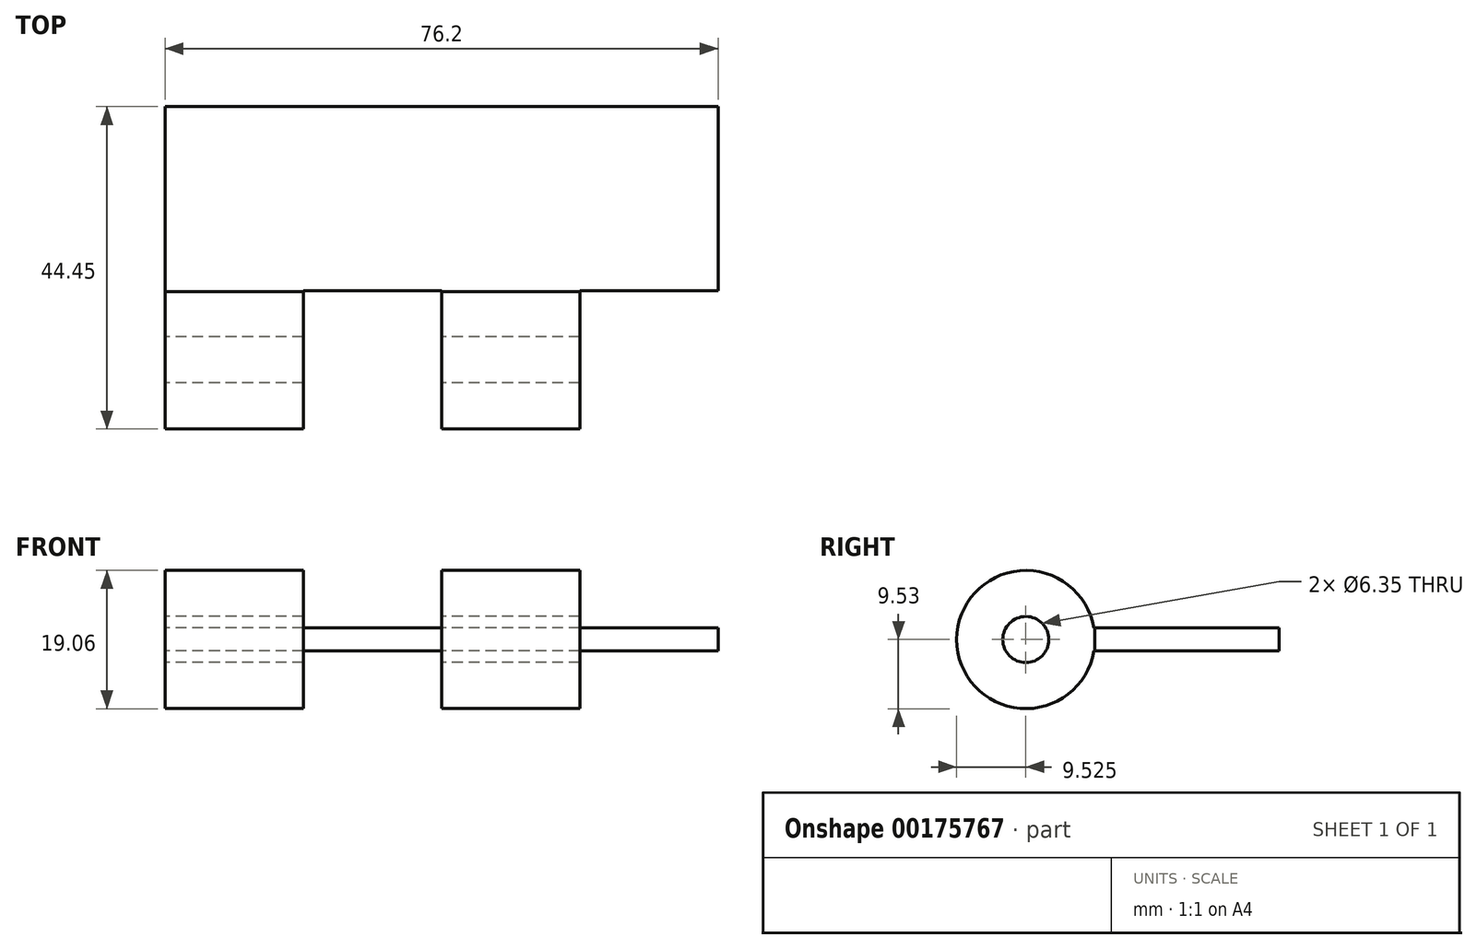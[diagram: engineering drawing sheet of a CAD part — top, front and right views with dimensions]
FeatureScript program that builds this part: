
annotation { "Feature Type Name" : "Feature", "Feature Type Description" : "" }
export const myFeature = defineFeature(function(context is Context, id is Id, definition is map)
    precondition{}
    {
        {
            var Q0;
            Q0=qCreatedBy(makeId("Top.planeOp"),FACE);
            var sketch = newSketch(context, id + "F0", { "sketchPlane" : qUnion([Q0])});
            skLineSegment(sketch, "E0.top", {"start": v(0, 31.75) * mm, "end": v(76.2, 31.75) * mm});
            skLineSegment(sketch, "E0.left", {"start": v(0, 0) * mm, "end": v(0, 31.75) * mm});
            skLineSegment(sketch, "E0.right", {"start": v(76.2, 6.35) * mm, "end": v(76.2, 31.75) * mm});
            skLineSegment(sketch, "E1", {"start": v(0, 0) * mm, "end": v(19.05, 0) * mm});
            skLineSegment(sketch, "E2", {"start": v(19.05, 0) * mm, "end": v(19.05, 6.35) * mm});
            skLineSegment(sketch, "E3", {"start": v(19.05, 6.35) * mm, "end": v(38.1, 6.35) * mm});
            skLineSegment(sketch, "E4", {"start": v(38.1, 6.35) * mm, "end": v(38.1, 0) * mm});
            skLineSegment(sketch, "E5", {"start": v(57.15, 0) * mm, "end": v(57.15, 6.35) * mm});
            skLineSegment(sketch, "E6", {"start": v(57.15, 6.35) * mm, "end": v(76.2, 6.35) * mm});
            skLineSegment(sketch, "E7.trimOffspring", {"start": v(38.1, 0) * mm, "end": v(57.15, 0) * mm});
            skSolve(sketch);
        }
        {
            var Q0;
            Q0=makeQuery(id+"F0.imprint","IMPRINT",FACE,{"disambiguationData":[TD([[makeQuery(id+"F0.imprint","IMPRINT",EDGE,{"derivedFrom":sQuery(id+"F0.wireOp",EDGE,"E0.top")}),-1.0]])]});
            extrude(context, id + "F1", {"entities" : qUnion([Q0]), "endBound" : BoundingType.SYMMETRIC, "depth" : 3.17 * mm});
        }
        {
            var Q0;
            Q0=qCreatedBy(makeId("Top.planeOp"),FACE);
            var sketch = newSketch(context, id + "F2", { "sketchPlane" : qUnion([Q0])});
            skLineSegment(sketch, "E8", {"start": v(0, -3.18) * mm, "end": v(90.4, -3.17) * mm, "construction": true});
            skLineSegment(sketch, "E9.bottom", {"start": v(57.15, 0) * mm, "end": v(38.1, 0) * mm});
            skLineSegment(sketch, "E9.top", {"start": v(57.15, 6.35) * mm, "end": v(38.1, 6.35) * mm});
            skLineSegment(sketch, "E9.left", {"start": v(57.15, 0) * mm, "end": v(57.15, 6.35) * mm});
            skLineSegment(sketch, "E9.right", {"start": v(38.1, 0) * mm, "end": v(38.1, 6.35) * mm});
            skLineSegment(sketch, "E10.bottom", {"start": v(19.05, 0) * mm, "end": v(0, 0) * mm});
            skLineSegment(sketch, "E10.top", {"start": v(19.05, 6.35) * mm, "end": v(0, 6.35) * mm});
            skLineSegment(sketch, "E10.left", {"start": v(19.05, 0) * mm, "end": v(19.05, 6.35) * mm});
            skLineSegment(sketch, "E10.right", {"start": v(0, 0) * mm, "end": v(0, 6.35) * mm});
            skSolve(sketch);
        }
        {
            var Q0;
            Q0 = qSketchRegion(id + "F2", true);
            var Q1;
            Q1=sQuery(id+"F2.wireOp",EDGE,"E8");
            revolve(context, id + "F3", {"operationType" : NewBodyOperationType.ADD, "entities" : qUnion([Q0]), "axis" : qUnion([Q1]), "revolveType" : RevolveType.FULL});
        }
    });
